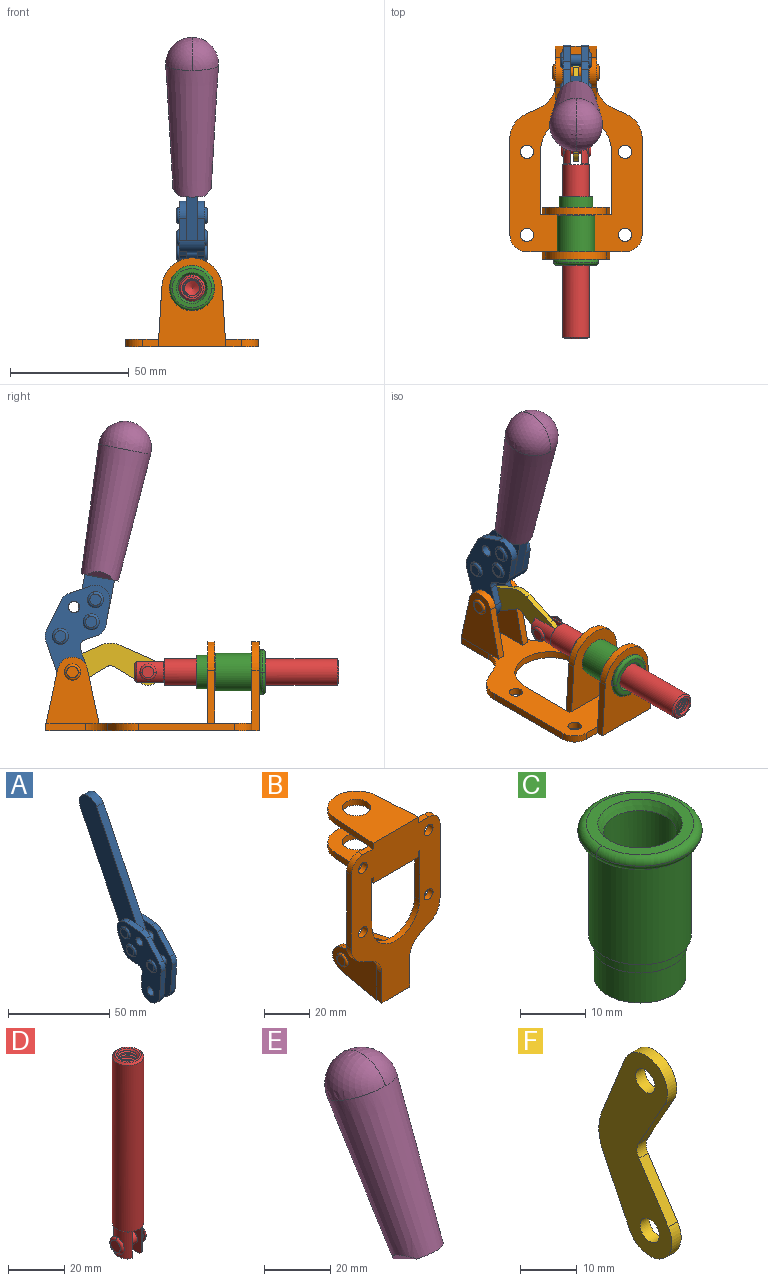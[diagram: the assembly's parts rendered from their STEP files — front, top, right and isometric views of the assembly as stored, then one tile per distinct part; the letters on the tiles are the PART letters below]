
ASSEMBLY  parts=6 mates=6
PART A: 59 faces, bbox 12.9x60.2x99.6 mm
  f0: torus R=2.39mm, axis (-1,0,0), area 14.9mm2, adj f20,f43,f51
  f1: torus R=2.39mm, axis (-1,0,0), area 14.9mm2, adj f19,f42,f51
  f2: torus R=2.39mm, axis (-1,0,0), area 14.9mm2, adj f18,f35,f51
  f3: torus R=2.39mm, axis (-1,0,0), area 14.9mm2, adj f14,f17,f23
  f4: torus R=2.39mm, axis (-1,0,0), area 14.9mm2, adj f13,f16,f23
  f5: torus R=2.39mm, axis (-1,0,0), area 14.9mm2, adj f12,f15,f23
  f6: cylinder r=2.39mm len=4.78mm, axis (1,0,0), area 46.5mm2, adj f48,f50,f51
  f7: cylinder r=2.39mm len=4.78mm, axis (1,0,0), area 46.5mm2, adj f50,f51
  f8: cylinder r=6.35mm len=12.68mm, axis (1,0,0), area 61.8mm2, adj f38,f39,f50,f51
  f9: cylinder r=2.39mm len=4.78mm, axis (-1,0,0), area 70.5mm2, adj f46,f50
  f10: cylinder r=2.39mm len=4.78mm, axis (-1,0,0), area 46.5mm2, adj f23,f45,f46
  f11: cylinder r=2.39mm len=4.78mm, axis (-1,0,0), area 46.5mm2, adj f23,f46
  f12: plane 4.78x4.78mm, normal (1,0,0), area 17.9mm2, adj f5,f15
  f13: plane 4.78x4.78mm, normal (1,0,0), area 17.9mm2, adj f4,f16
  f14: plane 4.78x4.78mm, normal (1,0,0), area 17.9mm2, adj f3,f17
  f15: torus R=2.39mm, axis (-1,0,0), area 14.9mm2, adj f5,f12,f23
  f16: torus R=2.39mm, axis (-1,0,0), area 14.9mm2, adj f4,f13,f23
  f17: torus R=2.39mm, axis (-1,0,0), area 14.9mm2, adj f3,f14,f23
  f18: plane 4.78x4.78mm, normal (-1,0,0), area 17.9mm2, adj f2,f35
  f19: plane 4.78x4.78mm, normal (-1,0,0), area 17.9mm2, adj f1,f42
  f20: plane 4.78x4.78mm, normal (-1,0,0), area 17.9mm2, adj f0,f43
  f21: plane 2.26x0.2mm, normal (1,0,0), area 0.2mm2, adj f31,f44
  f22: plane 2.26x0.2mm, normal (-1,0,0), area 0.2mm2, adj f41,f44
  f23: plane 39.37x30.77mm, normal (1,0,0), area 565.5mm2, adj f3,f4,f5,f10,f11,f15,f16,f17
  f24: cylinder r=6.1mm len=4.15mm, axis (-1,0,0), area 14.7mm2, adj f23,f25,f32,f46
  f25: plane 10.25x9.01mm, normal (0,-0.75,0.66), area 42.3mm2, adj f23,f24,f26,f46
  f26: cylinder r=6.35mm len=4.64mm, axis (-1,0,0), area 15.6mm2, adj f23,f25,f27,f46
  f27: plane 15.84x3.1mm, normal (0,-1,-0.07), area 49.2mm2, adj f23,f26,f28,f46
  f28: cylinder r=6.35mm len=12.68mm, axis (-1,0,0), area 61.8mm2, adj f23,f27,f29,f46
  f29: plane 8.11x3.1mm, normal (0,1,0.07), area 25.2mm2, adj f23,f28,f30,f46
  f30: cylinder r=3.05mm len=3.25mm, axis (-1,0,0), area 14.8mm2, adj f23,f29,f31,f46
  f31: plane 5.99x3.1mm, normal (0,0.07,-1), area 18.6mm2, adj f21,f23,f30,f44,f46
  f32: plane 9.5x3.1mm, normal (0,-0.07,1), area 29.5mm2, adj f23,f24,f33,f46,f47
  f33: cylinder r=6.1mm len=8.63mm, axis (-1,0,0), area 39.1mm2, adj f23,f32,f34,f47
  f34: plane 8.65x3.96mm, normal (0,0.91,-0.42), area 29.5mm2, adj f23,f33,f44,f47
  f35: torus R=2.39mm, axis (-1,0,0), area 14.9mm2, adj f2,f18,f51
  f36: plane 10.25x9.01mm, normal (0,-0.75,0.66), area 42.3mm2, adj f37,f49,f50,f51
  f37: cylinder r=6.35mm len=4.64mm, axis (1,0,0), area 15.6mm2, adj f36,f38,f50,f51
  f38: plane 15.84x3.1mm, normal (0,-1,-0.07), area 49.2mm2, adj f8,f37,f50,f51
  f39: plane 8.11x3.1mm, normal (0,1,0.07), area 25.2mm2, adj f8,f40,f50,f51
  f40: cylinder r=3.05mm len=3.25mm, axis (1,0,0), area 14.8mm2, adj f39,f41,f50,f51
  f41: plane 5.99x3.1mm, normal (0,0.07,-1), area 18.6mm2, adj f22,f40,f44,f50,f51
  f42: torus R=2.39mm, axis (-1,0,0), area 14.9mm2, adj f1,f19,f51
  f43: torus R=2.39mm, axis (-1,0,0), area 14.9mm2, adj f0,f20,f51
  f44: cylinder r=6.35mm len=12.12mm, axis (-1,0,0), area 128.9mm2, adj f21,f22,f23,f31,f34,f41,f46,f47
  f45: plane 2.65x1.35mm, normal (1,0,0), area 1mm2, adj f10,f55
  f46: plane 39.08x20.42mm, normal (-1,0,0), area 412.5mm2, adj f9,f10,f11,f24,f25,f26,f27,f28
  f47: plane 77.62x39.82mm, normal (1,0,0), area 850mm2, adj f32,f33,f34,f44,f53,f54,f55
  f48: plane 2.65x1.35mm, normal (-1,0,0), area 1mm2, adj f6,f55
  f49: cylinder r=6.1mm len=4.15mm, axis (1,0,0), area 14.7mm2, adj f36,f50,f51,f56
  f50: plane 39.08x20.42mm, normal (1,0,0), area 412.5mm2, adj f6,f7,f8,f9,f36,f37,f38,f39
  f51: plane 39.37x30.77mm, normal (-1,0,0), area 565.5mm2, adj f0,f1,f2,f6,f7,f8,f35,f36
  f52: plane 8.65x3.96mm, normal (0,0.91,-0.42), area 29.5mm2, adj f44,f51,f57,f58
  f53: plane 68.49x33.4mm, normal (0,0.9,-0.44), area 358.1mm2, adj f44,f47,f54,f58
  f54: cylinder r=6.35mm len=12.06mm, axis (1,0,0), area 93.7mm2, adj f47,f53,f55,f58
  f55: plane 68.49x33.4mm, normal (0,-0.9,0.44), area 358.1mm2, adj f44,f45,f46,f47,f48,f50,f54,f58
  f56: plane 9.5x3.1mm, normal (0,-0.07,1), area 29.5mm2, adj f49,f50,f51,f57,f58
  f57: cylinder r=6.1mm len=8.63mm, axis (1,0,0), area 39.1mm2, adj f51,f52,f56,f58
  f58: plane 77.62x39.82mm, normal (-1,0,0), area 850mm2, adj f44,f52,f53,f54,f55,f56,f57
PART B: 55 faces, bbox 55.7x37.4x89.8 mm
  f0: torus R=2.41mm, axis (-1,0,0), area 15mm2, adj f11,f15,f25
  f1: torus R=2.41mm, axis (-1,0,0), area 15mm2, adj f10,f12,f22
  f2: cylinder r=2.78mm len=5.56mm, axis (0,-1,0), area 54.2mm2, adj f30,f54
  f3: cylinder r=14.99mm len=29.97mm, axis (0,-1,0), area 145.9mm2, adj f30,f49,f53,f54
  f4: cylinder r=2.78mm len=5.56mm, axis (0,-1,0), area 54.2mm2, adj f30,f54
  f5: cylinder r=2.78mm len=5.56mm, axis (0,-1,0), area 54.2mm2, adj f30,f54
  f6: cylinder r=2.78mm len=5.56mm, axis (0,-1,0), area 54.2mm2, adj f30,f54
  f7: cylinder r=6.35mm len=12.7mm, axis (0,0,1), area 123.6mm2, adj f27,f51
  f8: cylinder r=6.35mm len=12.7mm, axis (0,0,-1), area 124.7mm2, adj f21,f35
  f9: cylinder r=2.41mm len=11.18mm, axis (-1,0,0), area 169.4mm2, adj f16,f19
  f10: plane 4.83x4.83mm, normal (1,0,0), area 18.3mm2, adj f1,f12
  f11: plane 4.83x4.83mm, normal (-1,0,0), area 18.3mm2, adj f0,f15
  f12: torus R=2.41mm, axis (-1,0,0), area 15mm2, adj f1,f10,f22
  f13: cylinder r=6.35mm len=12.41mm, axis (1,0,0), area 53.4mm2, adj f18,f19,f22,f23
  f14: cylinder r=6.35mm len=12.41mm, axis (-1,0,0), area 53.4mm2, adj f16,f17,f24,f25
  f15: torus R=2.41mm, axis (-1,0,0), area 15mm2, adj f0,f11,f25
  f16: plane 27.86x22.35mm, normal (1,0,0), area 425.4mm2, adj f9,f14,f17,f24,f30
  f17: plane 22.86x4.97mm, normal (0,0.21,0.98), area 72.5mm2, adj f14,f16,f25,f30
  f18: plane 22.86x4.97mm, normal (0,0.21,0.98), area 72.5mm2, adj f13,f19,f22,f30
  f19: plane 27.86x22.35mm, normal (-1,0,0), area 425.4mm2, adj f9,f13,f18,f23,f30
  f20: cylinder r=12.7mm len=25.35mm, axis (0,0,-1), area 119.8mm2, adj f21,f34,f35,f36
  f21: plane 34.21x28.07mm, normal (0,0,-1), area 702.4mm2, adj f8,f20,f30,f34,f36
  f22: plane 27.96x22.45mm, normal (1,0,0), area 407.2mm2, adj f1,f12,f13,f18,f23,f30,f42,f43
  f23: plane 22.86x4.97mm, normal (0,0.21,-0.98), area 72.5mm2, adj f13,f19,f22,f44
  f24: plane 22.86x4.97mm, normal (0,0.21,-0.98), area 72.5mm2, adj f14,f16,f25,f44
  f25: plane 27.86x22.35mm, normal (-1,0,0), area 407.1mm2, adj f0,f14,f15,f17,f24,f30,f45,f46
  f26: plane 3.1x0.95mm, normal (0,0,-1), area 2.7mm2, adj f30,f49,f50,f54
  f27: plane 34.21x28.07mm, normal (0,0,1), area 702.4mm2, adj f7,f28,f30,f50,f52
  f28: cylinder r=12.7mm len=25.35mm, axis (0,0,1), area 118.8mm2, adj f27,f50,f51,f52
  f29: plane 3.1x0.95mm, normal (0,0,-1), area 2.7mm2, adj f30,f52,f53,f54
  f30: plane 86.54x55.63mm, normal (0,1,0), area 2362.9mm2, adj f2,f3,f4,f5,f6,f16,f17,f18
  f31: plane 40.56x3.1mm, normal (-1,0,0), area 125.7mm2, adj f30,f32,f48,f54
  f32: cylinder r=7.11mm len=7.11mm, axis (0,-1,0), area 34.6mm2, adj f30,f31,f33,f54
  f33: plane 6.67x3.1mm, normal (0,0,1), area 20.4mm2, adj f30,f32,f34,f54
  f34: plane 25.39x3.13mm, normal (-1,0.06,0), area 79.5mm2, adj f20,f21,f33,f35,f54
  f35: plane 37.31x28.45mm, normal (0,0,1), area 789.9mm2, adj f8,f20,f34,f36,f54
  f36: plane 25.39x3.13mm, normal (1,0.06,0), area 79.5mm2, adj f20,f21,f35,f37,f54
  f37: plane 6.67x3.1mm, normal (0,0,1), area 20.4mm2, adj f30,f36,f38,f54
  f38: cylinder r=7.11mm len=7.11mm, axis (0,-1,0), area 34.6mm2, adj f30,f37,f39,f54
  f39: plane 40.56x3.1mm, normal (1,0,0), area 125.7mm2, adj f30,f38,f40,f54
  f40: cylinder r=11.18mm len=10.16mm, axis (0,-1,0), area 39.5mm2, adj f30,f39,f41,f54
  f41: plane 6.09x3.1mm, normal (0.42,0,-0.91), area 20.8mm2, adj f30,f40,f42,f54
  f42: cylinder r=11.18mm len=9.41mm, axis (0,-1,0), area 37.2mm2, adj f22,f30,f41,f43,f54
  f43: plane 16.5x3.1mm, normal (1,0,0), area 51.1mm2, adj f22,f42,f44,f54
  f44: plane 17.37x3.1mm, normal (0,0,-1), area 53.8mm2, adj f23,f24,f30,f43,f45,f54
  f45: plane 16.5x3.1mm, normal (-1,0,0), area 51.1mm2, adj f25,f44,f46,f54
  f46: cylinder r=11.18mm len=9.41mm, axis (0,-1,0), area 37.2mm2, adj f25,f30,f45,f47,f54
  f47: plane 6.09x3.1mm, normal (-0.42,0,-0.91), area 20.8mm2, adj f30,f46,f48,f54
  f48: cylinder r=11.18mm len=10.16mm, axis (0,-1,0), area 39.5mm2, adj f30,f31,f47,f54
  f49: plane 26.54x3.1mm, normal (-1,0,0), area 82.3mm2, adj f3,f26,f30,f54
  f50: plane 25.39x3.1mm, normal (1,0.06,0), area 78.8mm2, adj f26,f27,f28,f51,f54
  f51: plane 37.31x28.45mm, normal (0,0,-1), area 789.9mm2, adj f7,f28,f50,f52,f54
  f52: plane 25.39x3.1mm, normal (-1,0.06,0), area 78.8mm2, adj f27,f28,f29,f51,f54
  f53: plane 26.54x3.1mm, normal (1,0,0), area 82.3mm2, adj f3,f29,f30,f54
  f54: plane 89.66x55.63mm, normal (0,-1,0), area 2678.5mm2, adj f2,f3,f4,f5,f6,f26,f29,f31
PART C: 15 faces, bbox 20.6x20.6x28.7 mm
  f0: torus R=8.26mm, axis (0,0,1), area 56.8mm2, adj f1,f10,f12
  f1: torus R=8.26mm, axis (0,0,1), area 56.8mm2, adj f0,f6,f13
  f2: cylinder r=5.59mm len=25.91mm, axis (0,0,1), area 909.6mm2, adj f3,f4
  f3: cone r=6.86mm half-angle=45deg, axis (0,0,-1), area 70.2mm2, adj f2,f14
  f4: cone r=6.47mm half-angle=30deg, axis (0,0,1), area 66.7mm2, adj f2,f13
  f5: cylinder r=7.04mm len=14.07mm, axis (0,0,1), area 252.6mm2, adj f11,f14
  f6: torus R=8.26mm, axis (0,0,1), area 56.8mm2, adj f1,f12,f13
  f7: cylinder r=7.16mm len=14.33mm, axis (0,0,1), area 91.5mm2, adj f9,f11
  f8: cylinder r=7.86mm len=18.42mm, axis (0,0,1), area 909.6mm2, adj f9,f10
  f9: plane 15.72x15.72mm, normal (0,0,-1), area 33mm2, adj f7,f8
  f10: plane 16.51x16.51mm, normal (0,0,-1), area 19.9mm2, adj f0,f8,f12
  f11: plane 14.33x14.33mm, normal (0,0,-1), area 5.7mm2, adj f5,f7
  f12: torus R=8.26mm, axis (0,0,1), area 56.8mm2, adj f0,f6,f10
  f13: plane 16.51x16.51mm, normal (0,0,1), area 82.7mm2, adj f1,f4,f6
  f14: plane 14.07x14.07mm, normal (0,0,-1), area 7.8mm2, adj f3,f5
PART D: 48 faces, bbox 12.6x11.1x86.1 mm
  f0: torus R=2.41mm, axis (-1,0,0), area 15mm2, adj f30,f32,f34
  f1: torus R=2.41mm, axis (-1,0,0), area 15mm2, adj f29,f31,f33
  f2: cylinder r=5.54mm len=72.39mm, axis (0,0,1), area 2518.5mm2, adj f3,f4,f42,f43
  f3: cone r=5.54mm half-angle=45deg, axis (0,0,1), area 7.6mm2, adj f2,f5,f41
  f4: cone r=5.54mm half-angle=45deg, axis (0,0,-1), area 34.9mm2, adj f2,f39
  f5: cylinder r=5.08mm len=11.48mm, axis (0,0,1), area 108.3mm2, adj f3,f7,f8,f41
  f6: cylinder r=2.41mm len=4.83mm, axis (-1,0,0), area 71.2mm2, adj f40,f41
  f7: cylinder r=2.41mm len=4.83mm, axis (-1,0,0), area 7.6mm2, adj f5,f34
  f8: cone r=5.08mm half-angle=45deg, axis (0,0,1), area 10.6mm2, adj f5,f37,f41
  f9: cone r=3.98mm half-angle=45deg, axis (0,0,1), area 17.6mm2, adj f27,f39,f45,f46,f47
  f10: cylinder r=2.41mm len=4.83mm, axis (-1,0,0), area 7.6mm2, adj f33,f38
  f11: cylinder r=3.2mm len=6.4mm, axis (0,0,1), area 78.4mm2, adj f12,f28,f44,f45,f47
  f12: cylinder r=3.2mm len=6.4mm, axis (0,0,1), area 10.5mm2, adj f11,f13,f45,f47
  f13: cylinder r=3.2mm len=6.4mm, axis (0,0,1), area 10.5mm2, adj f12,f14,f45,f47
  f14: cylinder r=3.2mm len=6.4mm, axis (0,0,1), area 10.5mm2, adj f13,f15,f45,f47
  f15: cylinder r=3.2mm len=6.4mm, axis (0,0,1), area 10.5mm2, adj f14,f16,f45,f47
  f16: cylinder r=3.2mm len=6.4mm, axis (0,0,1), area 10.5mm2, adj f15,f17,f45,f47
  f17: cylinder r=3.2mm len=6.4mm, axis (0,0,1), area 10.5mm2, adj f16,f18,f45,f47
  f18: cylinder r=3.2mm len=6.4mm, axis (0,0,1), area 10.5mm2, adj f17,f19,f45,f47
  f19: cylinder r=3.2mm len=6.4mm, axis (0,0,1), area 10.5mm2, adj f18,f20,f45,f47
  f20: cylinder r=3.2mm len=6.4mm, axis (0,0,1), area 10.5mm2, adj f19,f21,f45,f47
  f21: cylinder r=3.2mm len=6.4mm, axis (0,0,1), area 10.5mm2, adj f20,f22,f45,f47
  f22: cylinder r=3.2mm len=6.4mm, axis (0,0,1), area 10.5mm2, adj f21,f23,f45,f47
  f23: cylinder r=3.2mm len=6.4mm, axis (0,0,1), area 10.5mm2, adj f22,f24,f45,f47
  f24: cylinder r=3.2mm len=6.4mm, axis (0,0,1), area 10.5mm2, adj f23,f25,f45,f47
  f25: cylinder r=3.2mm len=6.4mm, axis (0,0,1), area 10.5mm2, adj f24,f26,f45,f47
  f26: cylinder r=3.2mm len=6.4mm, axis (0,0,1), area 10.5mm2, adj f25,f27,f45,f47
  f27: cylinder r=3.2mm len=6.4mm, axis (0,0,1), area 7.4mm2, adj f9,f26,f45,f47
  f28: cone r=3.2mm half-angle=60deg, axis (0,0,1), area 37.2mm2, adj f11
  f29: plane 4.83x4.83mm, normal (-1,0,0), area 18.3mm2, adj f1,f31
  f30: plane 4.83x4.83mm, normal (1,0,0), area 18.3mm2, adj f0,f32
  f31: torus R=2.41mm, axis (-1,0,0), area 15mm2, adj f1,f29,f33
  f32: torus R=2.41mm, axis (-1,0,0), area 15mm2, adj f0,f30,f34
  f33: plane 6.83x6.83mm, normal (1,0,0), area 18.3mm2, adj f1,f10,f31
  f34: plane 6.83x6.83mm, normal (-1,0,0), area 18.3mm2, adj f0,f7,f32
  f35: cone r=5.08mm half-angle=45deg, axis (0,0,1), area 10.6mm2, adj f36,f38,f40
  f36: plane 7.25x1.97mm, normal (0,0,-1), area 10mm2, adj f35,f40
  f37: plane 7.25x1.97mm, normal (0,0,-1), area 10mm2, adj f8,f41
  f38: cylinder r=5.08mm len=11.48mm, axis (0,0,1), area 108.3mm2, adj f10,f35,f40,f42
  f39: plane 9.55x9.55mm, normal (0,0,1), area 22mm2, adj f4,f9
  f40: plane 12.76x10.09mm, normal (1,0,0), area 95.7mm2, adj f6,f35,f36,f38,f42,f43
  f41: plane 12.76x10.09mm, normal (-1,0,0), area 95.7mm2, adj f3,f5,f6,f8,f37,f43
  f42: cone r=5.54mm half-angle=45deg, axis (0,0,1), area 7.6mm2, adj f2,f38,f40
  f43: plane 11.07x4.7mm, normal (0,0,-1), area 50.4mm2, adj f2,f40,f41
  f44: plane 0.89x0.62mm, normal (-1,0,0), area 0.3mm2, adj f11,f45,f46,f47
  f45: bspline ~24.8x7.63mm, area 266.6mm2, adj f9,f11,f12,f13,f14,f15,f16,f17
  f46: bspline ~24.87x7.63mm, area 73.6mm2, adj f9,f44,f45,f47
  f47: bspline ~24.98x7.63mm, area 272.5mm2, adj f9,f11,f12,f13,f14,f15,f16,f17
PART E: 11 faces, bbox 22.3x42.6x64.5 mm
  f0: sphere r=11.13mm, area 411.4mm2, adj f1,f8
  f1: cone r=11.11mm half-angle=3.3deg, axis (0,0.44,0.9), area 3251.8mm2, adj f0,f7,f8,f9,f10
  f2: cylinder r=6.16mm len=11.7mm, axis (1,0,0), area 89.5mm2, adj f3,f4,f5,f6
  f3: plane 60.23x36.75mm, normal (-1,0,0), area 763.6mm2, adj f2,f4,f6,f10
  f4: plane 51.37x25.05mm, normal (0,0.9,-0.44), area 264.2mm2, adj f2,f3,f5,f10
  f5: plane 60.23x36.75mm, normal (1,0,0), area 763.6mm2, adj f2,f4,f6,f10
  f6: plane 51.37x25.05mm, normal (0,-0.9,0.44), area 264.2mm2, adj f2,f3,f5,f10
  f7: plane 9.95x5.95mm, normal (0.71,-0.31,-0.64), area 25.8mm2, adj f1,f10
  f8: sphere r=11.13mm, area 411.4mm2, adj f0,f1
  f9: plane 9.95x5.95mm, normal (-0.71,-0.31,-0.64), area 25.8mm2, adj f1,f10
  f10: plane 14.27x11.38mm, normal (0,-0.44,-0.9), area 106.7mm2, adj f1,f3,f4,f5,f6,f7,f9
PART F: 12 faces, bbox 2.3x18.2x42.8 mm
  f0: cylinder r=2.4mm len=4.8mm, axis (1,0,0), area 34.9mm2, adj f4,f11
  f1: cylinder r=10.41mm len=8.47mm, axis (1,0,0), area 20.2mm2, adj f4,f9,f10,f11
  f2: cylinder r=3.05mm len=3.16mm, axis (1,0,0), area 7.7mm2, adj f4,f6,f7,f11
  f3: cylinder r=2.4mm len=4.8mm, axis (1,0,0), area 34.9mm2, adj f4,f11
  f4: plane 42.81x18.23mm, normal (-1,0,0), area 414.1mm2, adj f0,f1,f2,f3,f5,f6,f7,f8
  f5: cylinder r=5.54mm len=10.67mm, axis (1,0,0), area 41.8mm2, adj f4,f6,f10,f11
  f6: plane 11.66x6.53mm, normal (0,-0.87,-0.49), area 30.9mm2, adj f2,f4,f5,f11
  f7: plane 11.17x7.33mm, normal (0,-0.84,0.55), area 30.9mm2, adj f2,f4,f8,f11
  f8: cylinder r=5.54mm len=10.51mm, axis (1,0,0), area 41.8mm2, adj f4,f7,f9,f11
  f9: plane 13.67x6.67mm, normal (0,0.9,-0.44), area 35.1mm2, adj f1,f4,f8,f11
  f10: plane 14.1x5.7mm, normal (0,0.93,0.37), area 35.1mm2, adj f1,f4,f5,f11
  f11: plane 42.81x18.23mm, normal (1,0,0), area 414.1mm2, adj f0,f1,f2,f3,f5,f6,f7,f8
PLACE A rot(axis=(0,0.13,0.99),180deg) t=(0,73.6,49.24)mm
PLACE B rot(axis=(1,0,0),90deg) t=(0,9.43,0)mm fixed
PLACE C rot(axis=(1,0,0),90deg) t=(0,9.43,0)mm
PLACE D rot(axis=(1,0,0),90deg) t=(0,25.25,0)mm
PLACE E rot(axis=(0,0.13,0.99),180deg) t=(0.04,73.6,49.24)mm
PLACE F rot(axis=(1,0,0),92deg) t=(0,26.1,0.55)mm
MATE fastened E.f2 <-> A.f54  axis (-1,0,0) through (2.35,19.16,120.54)mm
MATE revolute F.f3 <-> A.f7  axis (1,0,0) through (0,41.52,24.61)mm
MATE fastened B.f7 <-> C.f2  axis (0,-1,0) through (0,-36.96,24.61)mm
MATE revolute B.f0 <-> A.f7  axis (-1,0,0) through (0,41.52,24.61)mm
MATE slider D.f2 <-> C.f2  axis (0,-1,0) through (0,-33.53,24.61)mm
MATE revolute D.f6 <-> F.f5  axis (-1,0,0) through (0,9.77,24.61)mm
